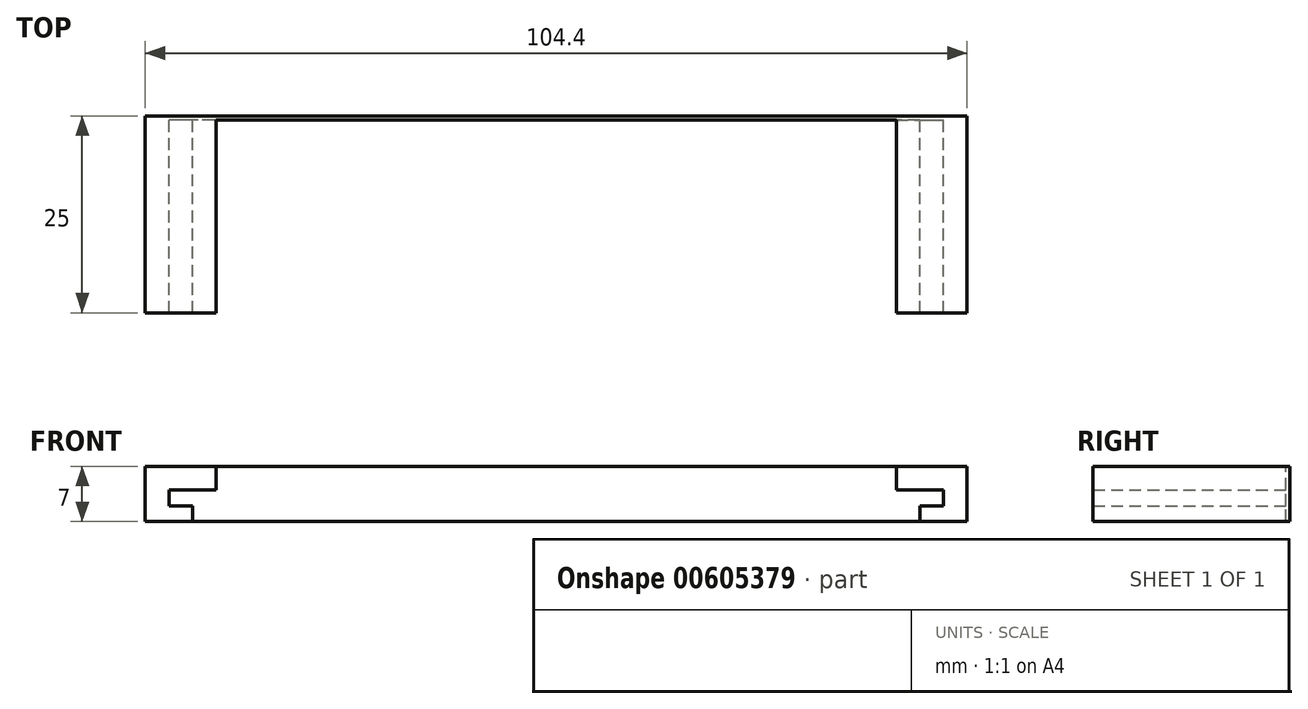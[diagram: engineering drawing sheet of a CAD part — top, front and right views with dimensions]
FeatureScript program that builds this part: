
annotation { "Feature Type Name" : "Feature", "Feature Type Description" : "" }
export const myFeature = defineFeature(function(context is Context, id is Id, definition is map)
    precondition{}
    {
        {
            var Q0;
            Q0=qCreatedBy(makeId("Front.planeOp"),FACE);
            var sketch = newSketch(context, id + "F0", { "sketchPlane" : qUnion([Q0])});
            skLineSegment(sketch, "E0.bottom", {"start": v(-49.2, 3.5) * mm, "end": v(-43.2, 3.5) * mm});
            skLineSegment(sketch, "E0.top", {"start": v(-49.2, 0.5) * mm, "end": v(-43.2, 0.5) * mm});
            skLineSegment(sketch, "E0.left", {"start": v(-49.2, 3.5) * mm, "end": v(-49.2, 0.5) * mm});
            skLineSegment(sketch, "E0.right", {"start": v(-43.2, 3.5) * mm, "end": v(-43.2, 0.5) * mm});
            skLineSegment(sketch, "E1.bottom", {"start": v(-49.2, 3.5) * mm, "end": v(-52.2, 3.5) * mm});
            skLineSegment(sketch, "E1.top", {"start": v(-49.2, -3.5) * mm, "end": v(-52.2, -3.5) * mm});
            skLineSegment(sketch, "E1.left", {"start": v(-49.2, 3.5) * mm, "end": v(-49.2, -3.5) * mm});
            skLineSegment(sketch, "E1.right", {"start": v(-52.2, 3.5) * mm, "end": v(-52.2, -3.5) * mm});
            skLineSegment(sketch, "E2.bottom", {"start": v(-49.2, -1.5) * mm, "end": v(-46.2, -1.5) * mm});
            skLineSegment(sketch, "E2.top", {"start": v(-49.2, -3.5) * mm, "end": v(-46.2, -3.5) * mm});
            skLineSegment(sketch, "E2.left", {"start": v(-49.2, -1.5) * mm, "end": v(-49.2, -3.5) * mm});
            skLineSegment(sketch, "E2.right", {"start": v(-46.2, -1.5) * mm, "end": v(-46.2, -3.5) * mm});
            skLineSegment(sketch, "E3.MirrorCS", {"start": v(49.2, 3.5) * mm, "end": v(49.2, 0.5) * mm});
            skLineSegment(sketch, "E4.MirrorCS", {"start": v(46.2, -1.5) * mm, "end": v(46.2, -3.5) * mm});
            skLineSegment(sketch, "E5.MirrorCS", {"start": v(49.2, -1.5) * mm, "end": v(49.2, -3.5) * mm});
            skLineSegment(sketch, "E6.MirrorCS", {"start": v(49.2, -3.5) * mm, "end": v(46.2, -3.5) * mm});
            skLineSegment(sketch, "E7.MirrorCS", {"start": v(52.2, 3.5) * mm, "end": v(52.2, -3.5) * mm});
            skLineSegment(sketch, "E8.MirrorCS", {"start": v(49.2, 3.5) * mm, "end": v(49.2, -3.5) * mm});
            skLineSegment(sketch, "E9.MirrorCS", {"start": v(43.2, 3.5) * mm, "end": v(43.2, 0.5) * mm});
            skLineSegment(sketch, "E10.MirrorCS", {"start": v(49.2, -3.5) * mm, "end": v(52.2, -3.5) * mm});
            skLineSegment(sketch, "E11.MirrorCS", {"start": v(49.2, -1.5) * mm, "end": v(46.2, -1.5) * mm});
            skLineSegment(sketch, "E12.MirrorCS", {"start": v(49.2, 0.5) * mm, "end": v(43.2, 0.5) * mm});
            skLineSegment(sketch, "E13.MirrorCS", {"start": v(49.2, 3.5) * mm, "end": v(43.2, 3.5) * mm});
            skLineSegment(sketch, "E14.MirrorCS", {"start": v(49.2, 3.5) * mm, "end": v(52.2, 3.5) * mm});
            skPoint(sketch, "E15", {"position": v(-52.2, 0) * mm});
            skSolve(sketch);
        }
        {
            var Q0;
            Q0=qCreatedBy(makeId("Front.planeOp"),FACE);
            var sketch = newSketch(context, id + "F1", { "sketchPlane" : qUnion([Q0])});
            skLineSegment(sketch, "E16.bottom", {"start": v(52.2, 3.5) * mm, "end": v(-52.2, 3.5) * mm});
            skLineSegment(sketch, "E16.top", {"start": v(52.2, -3.5) * mm, "end": v(-52.2, -3.5) * mm});
            skLineSegment(sketch, "E16.left", {"start": v(52.2, 3.5) * mm, "end": v(52.2, -3.5) * mm});
            skLineSegment(sketch, "E16.right", {"start": v(-52.2, 3.5) * mm, "end": v(-52.2, -3.5) * mm});
            skSolve(sketch);
        }
        {
            var Q0;
            Q0 = qSketchRegion(id + "F1", true);
            extrude(context, id + "F2", {"entities" : qUnion([Q0]), "depth" : 0.5 * mm, "offsetDistance" : 25 * mm});
        }
        {
            var Q0;
            Q0 = qSketchRegion(id + "F0", true);
            extrude(context, id + "F3", {"entities" : qUnion([Q0]), "operationType" : NewBodyOperationType.ADD, "depth" : 25 * mm, "offsetDistance" : 25 * mm});
        }
    });
